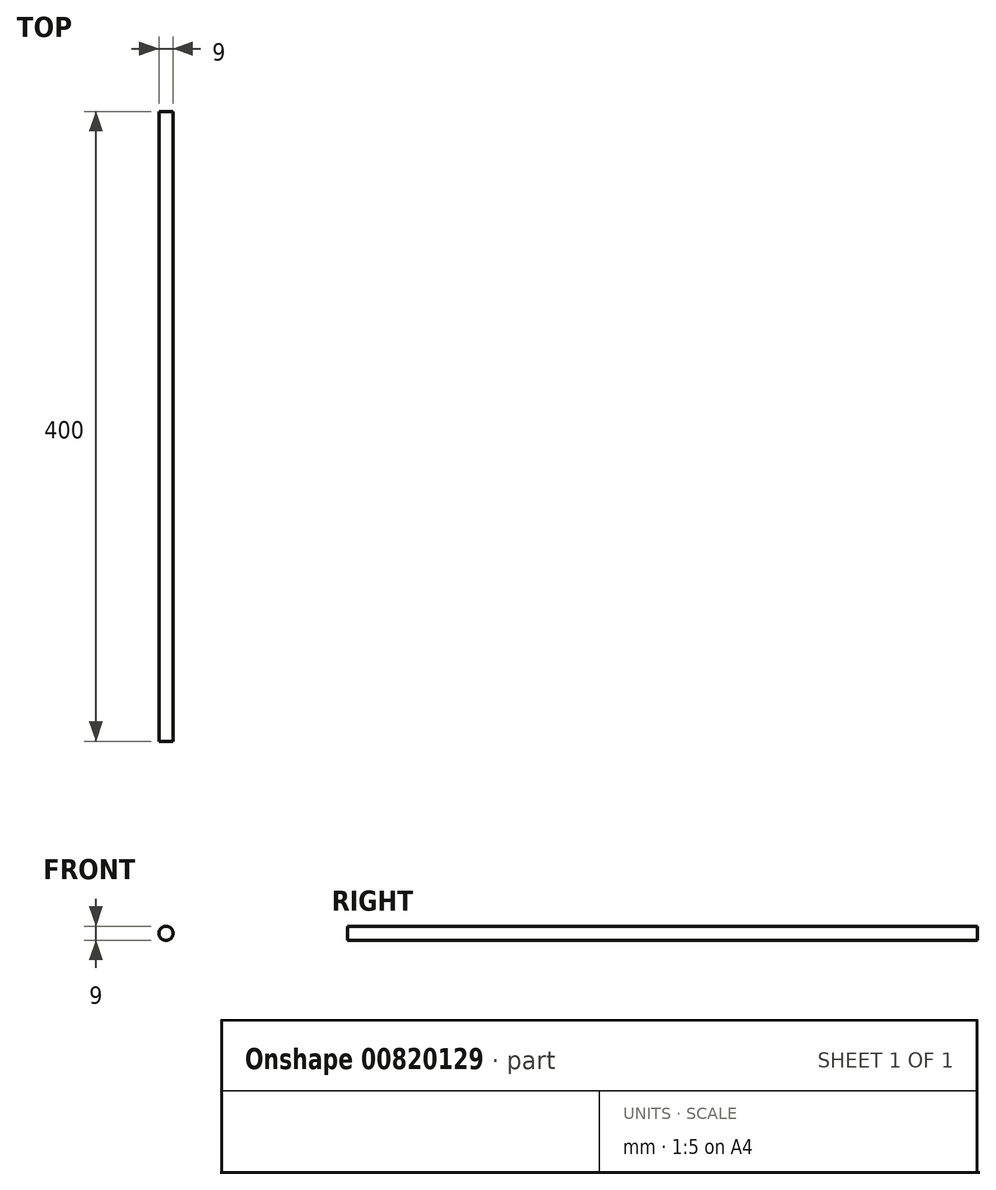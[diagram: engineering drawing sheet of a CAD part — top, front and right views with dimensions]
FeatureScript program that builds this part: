
annotation { "Feature Type Name" : "Feature", "Feature Type Description" : "" }
export const myFeature = defineFeature(function(context is Context, id is Id, definition is map)
    precondition{}
    {
        {
            var Q0;
            Q0=qCreatedBy(makeId("Front.planeOp"),FACE);
            var sketch = newSketch(context, id + "F0", { "sketchPlane" : qUnion([Q0])});
            skCircle(sketch, "E0", {"center": v(0, 0) * mm, "radius": 4.5 * mm});
            skSolve(sketch);
        }
        {
            var Q0;
            Q0=makeQuery(id+"F0.imprint","IMPRINT",FACE,{"disambiguationData":[TD([[makeQuery(id+"F0.imprint","IMPRINT",EDGE,{"derivedFrom":sQuery(id+"F0.wireOp",EDGE,"E0")}),1.0]])]});
            extrude(context, id + "F1", {"entities" : qUnion([Q0]), "depth" : 100 * mm, "offsetDistance" : 25 * mm, "hasSecondDirection" : true, "secondDirectionOppositeDirection" : true, "secondDirectionDepth" : 300 * mm});
        }
    });
